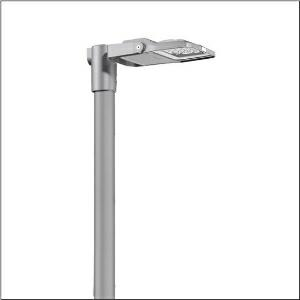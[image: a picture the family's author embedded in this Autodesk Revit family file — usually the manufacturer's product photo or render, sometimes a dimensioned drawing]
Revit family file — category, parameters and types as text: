
# Revit family: floodlight_fl_21_iq_micro___pl33t_5xa7762a4f3a_b73c
name_source: partatom
category: Lighting Fixtures
units: mm (PartAtom-declared; Revit-internal decimal feet)

## family parameters
Cut with Voids When Loaded = No
Host = Face
Light Source = No
Part Type = Normal
Room Calculation Point = No
Round Connector Dimension = Use Diameter
Shared = No

## types (1)
- --- (1 x LED, 3050 lm, 23.1 W, 4000K)
    Apparent Load = 23 VA
    CIE Flux Codes = 26 75 99 100 100
    Color Rendering = 70
    Color Temperature = 4000K
    Default Elevation = 1800 mm
    Description = Floodlight FL 21 iQ micro, floodlight, primary light control with lens, of PMMA, primary optical cover: protective disc, of toughened safety glass, transparent, light distribution: PL33T, light emission: direct distribution, installation type: surface-mounted, LED, High Power LED, rated luminous flux: 3.050lm, luminous efficacy: 132lm/W, light colour: 740, colour temperature: 4000K, control gear: iQ Street-Remote/DALI, control: Auto-Match, Temp-Guard, Night-Set, Smart-Wire, Desk-Remote (wireless, voltage-free reading and setting of iQ features in the workshop via application-optimized NFC function/RFID function), optimised constant luminous flux control (CLO 2.0), Street-Remote, with terminal, 6-pole, mains connection: 220..240V, AC, 50/60Hz, start of lifetime: 23W, end of service life: 24W, reduction: 11W, luminaire housing, of diecast aluminium, powder-coated, Siteco® metallic grey (DB 702S), corrosivity category C5 mid according to DIN EN ISO 12944, suitable for swimming pools, chlorine-resistant, sealing non-destructively replaceable, please order mast flange separately, mast bracket, of steel, galvanised, powder-coated, Siteco® metallic grey (DB 702S), protection rating (complete): IP66, insulation class (complete): insulation class II (safety insulation), certification: CE, ENEC, VDE, protection symbol: D, impact resistance: IK07, permissible operating ambient temperature: -40..+40°C, permissible operating ambient temperature for outdoor applications: -40..+50°C, standard: DIN EN 12944, LABS conformity tested according to VDMA 24364:2018-05, packaging unit: 1 piece

Light Distribution: PL33T
    Height = 65 mm
    Lamp = 1 x LED
    Lamp Light Flux = 3050 lm
    Lamp Power = 23.1 W
    Lamp count = 1
    Length = 312 mm
    Luminous efficacy = 132 lm/W
    Manufacturer = Siteco
    ModVariant = No
    Model = 5XA7762A4F3A
    Number of Poles = 1
    OnlyDefault = Yes
    Power Factor = 1
    Product Name = Floodlight FL 21 iQ micro | PL33T
    Product group = floodlight | pylon annexe
    ProductGroupID = 6200
    Protection Class = Protection class II
    Protection Degree = IP 66
    RLX_Detail_Level = 1
    RLX_Emergency_Light_Flux = 0 lm
    RLX_Emergency_Type = 0
    RLX_Emergency_Type_DB = No
    RlxData = <blob elided: 101937 chars, md5=6c0008a4>
    Socket = socket
    Standby Power = 0 W
    System Light Flux = 3050 lm
    System Power = 23 W
    Type Comments = factory setting: luminous flux: 100 % | dim-lin: 254 | 455 mA
    Type Image = l_1007121.jpg
    URL = http://relux.com
    VarID = @adj_147866
    Voltage = 0 V
    Weight = 0.00 kg
    Width = 230 mm

## geometry (parser evidence)
native form markers: Blend x4, Sweep x12
no freeform markers — native parametric forms only
